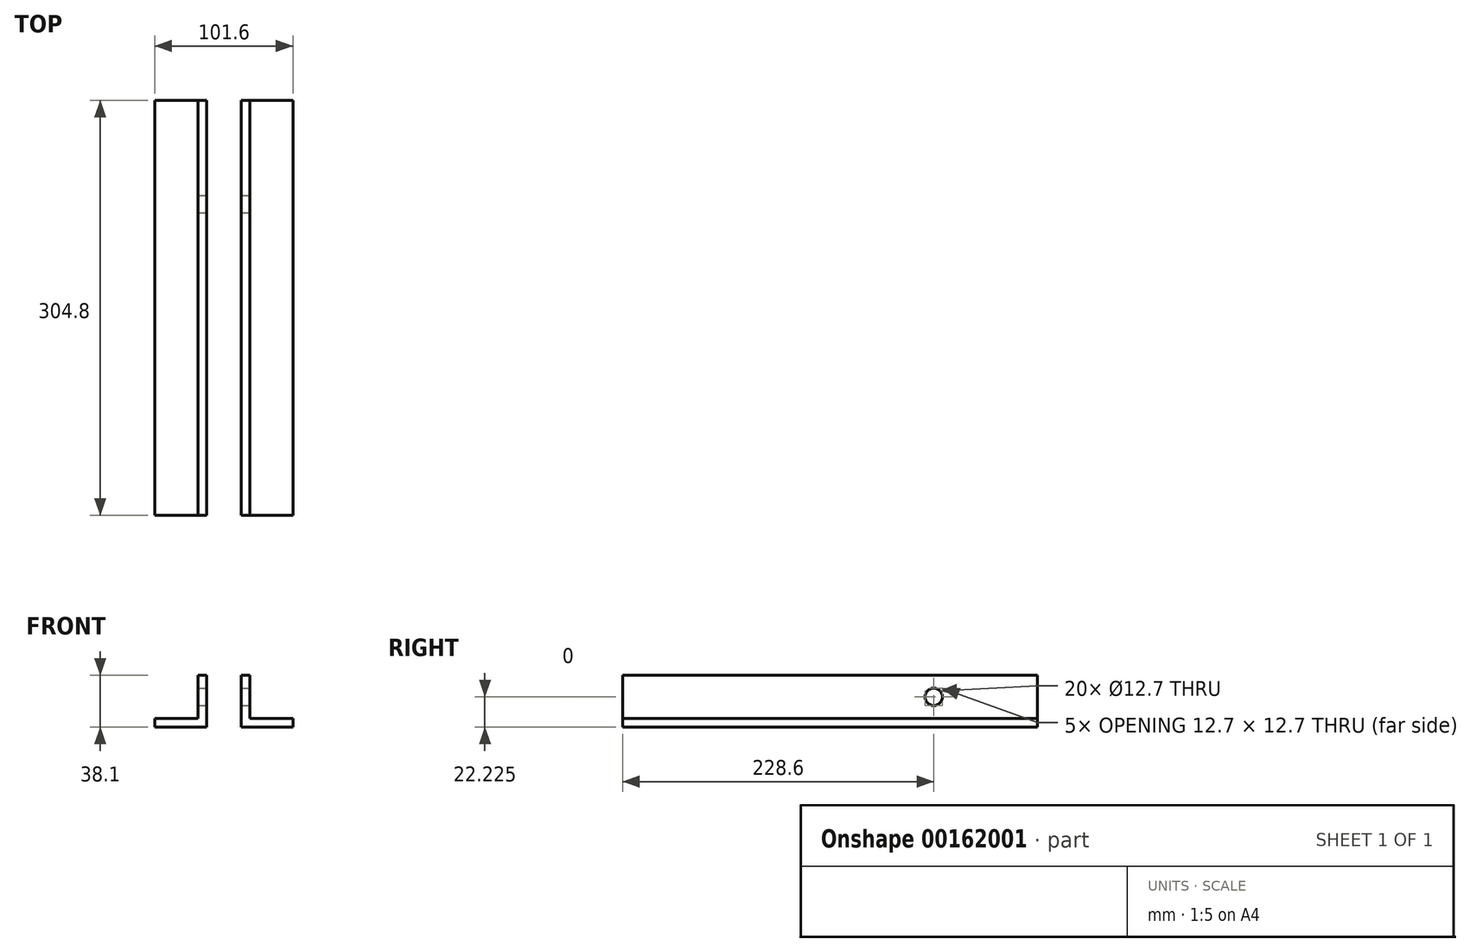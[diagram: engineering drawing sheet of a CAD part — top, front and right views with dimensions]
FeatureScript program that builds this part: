
annotation { "Feature Type Name" : "Feature", "Feature Type Description" : "" }
export const myFeature = defineFeature(function(context is Context, id is Id, definition is map)
    precondition{}
    {
        {
            var Q0;
            Q0=qCreatedBy(makeId("Front.planeOp"),FACE);
            var sketch = newSketch(context, id + "F0", { "sketchPlane" : qUnion([Q0])});
            skLineSegment(sketch, "E0", {"start": v(-12.7, 0) * mm, "end": v(-50.8, 0) * mm});
            skLineSegment(sketch, "E1", {"start": v(-50.8, 0) * mm, "end": v(-50.8, 6.35) * mm});
            skLineSegment(sketch, "E2", {"start": v(-50.8, 6.35) * mm, "end": v(-19.05, 6.35) * mm});
            skLineSegment(sketch, "E3", {"start": v(-19.05, 6.35) * mm, "end": v(-19.05, 38.1) * mm});
            skLineSegment(sketch, "E4", {"start": v(-19.05, 38.1) * mm, "end": v(-12.7, 38.1) * mm});
            skLineSegment(sketch, "E5", {"start": v(-12.7, 38.1) * mm, "end": v(-12.7, 0) * mm});
            skLineSegment(sketch, "E6.MirrorCS", {"start": v(12.7, 0) * mm, "end": v(50.8, 0) * mm});
            skLineSegment(sketch, "E7.MirrorCS", {"start": v(50.8, 0) * mm, "end": v(50.8, 6.35) * mm});
            skLineSegment(sketch, "E8.MirrorCS", {"start": v(50.8, 6.35) * mm, "end": v(19.05, 6.35) * mm});
            skLineSegment(sketch, "E9.MirrorCS", {"start": v(19.05, 6.35) * mm, "end": v(19.05, 38.1) * mm});
            skLineSegment(sketch, "E10.MirrorCS", {"start": v(19.05, 38.1) * mm, "end": v(12.7, 38.1) * mm});
            skLineSegment(sketch, "E11.MirrorCS", {"start": v(12.7, 38.1) * mm, "end": v(12.7, 0) * mm});
            skSolve(sketch);
        }
        {
            var Q0;
            Q0=makeQuery(id+"F0.imprint","IMPRINT",FACE,{"disambiguationData":[TD([[makeQuery(id+"F0.imprint","IMPRINT",EDGE,{"derivedFrom":sQuery(id+"F0.wireOp",EDGE,"E0")}),-1.0]])]});
            var Q1;
            Q1=makeQuery(id+"F0.imprint","IMPRINT",FACE,{"disambiguationData":[TD([[makeQuery(id+"F0.imprint","IMPRINT",EDGE,{"derivedFrom":sQuery(id+"F0.wireOp",EDGE,"E6.MirrorCS")}),1.0]])]});
            extrude(context, id + "F1", {"entities" : qUnion([Q0, Q1]), "depth" : 304.8 * mm});
        }
        {
            var Q0;
            Q0=makeQuery(id+"F1.opExtrude","SWEPT_FACE",FACE,{"disambiguationData":[OSD([sQuery(id+"F0.wireOp",EDGE,"E9.MirrorCS")])]});
            var sketch = newSketch(context, id + "F2", { "sketchPlane" : qUnion([Q0])});
            skCircle(sketch, "E12", {"center": v(-76.2, 22.22) * mm, "radius": 6.35 * mm});
            skSolve(sketch);
        }
        {
            var Q0;
            Q0=sQuery(id+"F2.wireOp",VERTEX,"E12.center");
            var Q1;
            Q1=makeQuery(id+"F1.opExtrude","SWEPT_BODY",BODY,{"disambiguationData":[OSD([sQuery(id+"F0.wireOp",EDGE,"E6.MirrorCS"),sQuery(id+"F0.wireOp",EDGE,"E7.MirrorCS"),sQuery(id+"F0.wireOp",EDGE,"E8.MirrorCS"),sQuery(id+"F0.wireOp",EDGE,"E9.MirrorCS"),sQuery(id+"F0.wireOp",EDGE,"E10.MirrorCS"),sQuery(id+"F0.wireOp",EDGE,"E11.MirrorCS")])]});
            var Q2;
            Q2=makeQuery(id+"F1.opExtrude","SWEPT_BODY",BODY,{"disambiguationData":[OSD([sQuery(id+"F0.wireOp",EDGE,"E0"),sQuery(id+"F0.wireOp",EDGE,"E1"),sQuery(id+"F0.wireOp",EDGE,"E2"),sQuery(id+"F0.wireOp",EDGE,"E3"),sQuery(id+"F0.wireOp",EDGE,"E4"),sQuery(id+"F0.wireOp",EDGE,"E5")])]});
            hole(context, id + "F3", {"style" : HoleStyle.SIMPLE, "endStyle" : HoleEndStyle.THROUGH, "holeDiameter" : 12.7 * mm, "locations" : qUnion([Q0]), "scope" : qUnion([Q1, Q2]), "isTappedThrough" : true});
        }
    });
